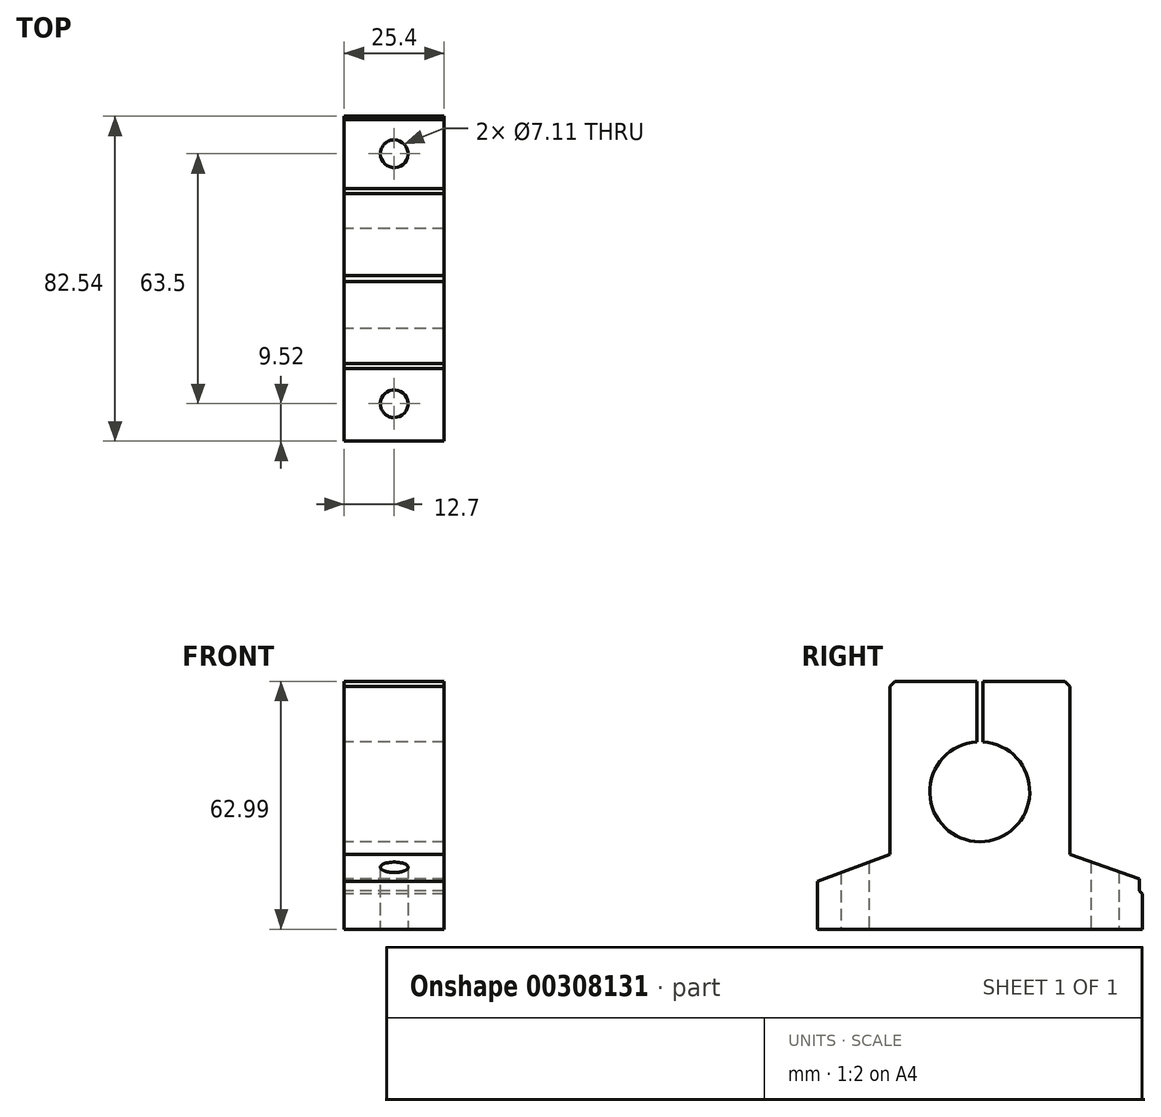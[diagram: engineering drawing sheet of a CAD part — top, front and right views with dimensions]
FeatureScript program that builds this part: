
annotation { "Feature Type Name" : "Feature", "Feature Type Description" : "" }
export const myFeature = defineFeature(function(context is Context, id is Id, definition is map)
    precondition{}
    {
        {
            var Q0;
            Q0=qCreatedBy(makeId("Right.planeOp"),FACE);
            var sketch = newSketch(context, id + "F0", { "sketchPlane" : qUnion([Q0])});
            skLineSegment(sketch, "E0", {"start": v(0.76, 17.64) * mm, "end": v(0.76, 33.02) * mm});
            skLineSegment(sketch, "E1", {"start": v(21.6, 33.02) * mm, "end": v(0.76, 33.02) * mm});
            skLineSegment(sketch, "E2", {"start": v(22.86, 31.75) * mm, "end": v(21.6, 33.02) * mm});
            skLineSegment(sketch, "E3", {"start": v(22.86, -10.92) * mm, "end": v(22.86, 31.75) * mm});
            skLineSegment(sketch, "E4", {"start": v(40.49, -17.22) * mm, "end": v(40.49, -20.27) * mm});
            skLineSegment(sketch, "E5", {"start": v(41.28, -29.97) * mm, "end": v(-41.28, -29.97) * mm});
            skLineSegment(sketch, "E6", {"start": v(-41.28, -17.78) * mm, "end": v(-41.28, -29.97) * mm});
            skLineSegment(sketch, "E7", {"start": v(-22.86, -10.92) * mm, "end": v(-41.28, -17.78) * mm});
            skLineSegment(sketch, "E8", {"start": v(-22.86, 31.75) * mm, "end": v(-22.86, -10.92) * mm});
            skLineSegment(sketch, "E9", {"start": v(-21.6, 33.02) * mm, "end": v(-22.86, 31.75) * mm});
            skLineSegment(sketch, "E10", {"start": v(-0.76, 33.02) * mm, "end": v(-0.76, 17.64) * mm});
            skLineSegment(sketch, "E11", {"start": v(-0.76, 33.02) * mm, "end": v(-21.6, 33.02) * mm});
            skLineSegment(sketch, "E12", {"start": v(40.49, -17.22) * mm, "end": v(22.86, -10.92) * mm});
            skArc(sketch, "E13", {"start": v(-0.76, 17.64) * mm, "mid": v(0, -7.74) * mm, "end": v(0.76, 17.64) * mm});
            skLineSegment(sketch, "E14", {"start": v(41.28, -21.06) * mm, "end": v(41.28, -29.97) * mm});
            skLineSegment(sketch, "E15", {"start": v(40.49, -20.27) * mm, "end": v(41.28, -21.06) * mm});
            skSolve(sketch);
        }
        {
            var Q0;
            Q0 = qSketchRegion(id + "F0", true);
            extrude(context, id + "F1", {"entities" : qUnion([Q0]), "endBound" : BoundingType.SYMMETRIC, "depth" : 25.4 * mm});
        }
        {
            var Q0;
            Q0=makeQuery(id+"F1.opExtrude","SWEPT_FACE",FACE,{"disambiguationData":[OSD([sQuery(id+"F0.wireOp",EDGE,"E5")])]});
            var sketch = newSketch(context, id + "F2", { "sketchPlane" : qUnion([Q0])});
            skCircle(sketch, "E16", {"center": v(0, 31.75) * mm, "radius": 3.56 * mm});
            skCircle(sketch, "E17", {"center": v(0, -31.75) * mm, "radius": 3.56 * mm});
            skLineSegment(sketch, "E18", {"start": v(0, 0) * mm, "end": v(-8.91, 0) * mm});
            skSolve(sketch);
        }
        {
            var Q0;
            Q0 = qSketchRegion(id + "F2", true);
            extrude(context, id + "F3", {"entities" : qUnion([Q0]), "operationType" : NewBodyOperationType.REMOVE, "endBound" : BoundingType.THROUGH_ALL, "oppositeDirection" : true, "depth" : 25.4 * mm});
        }
    });
